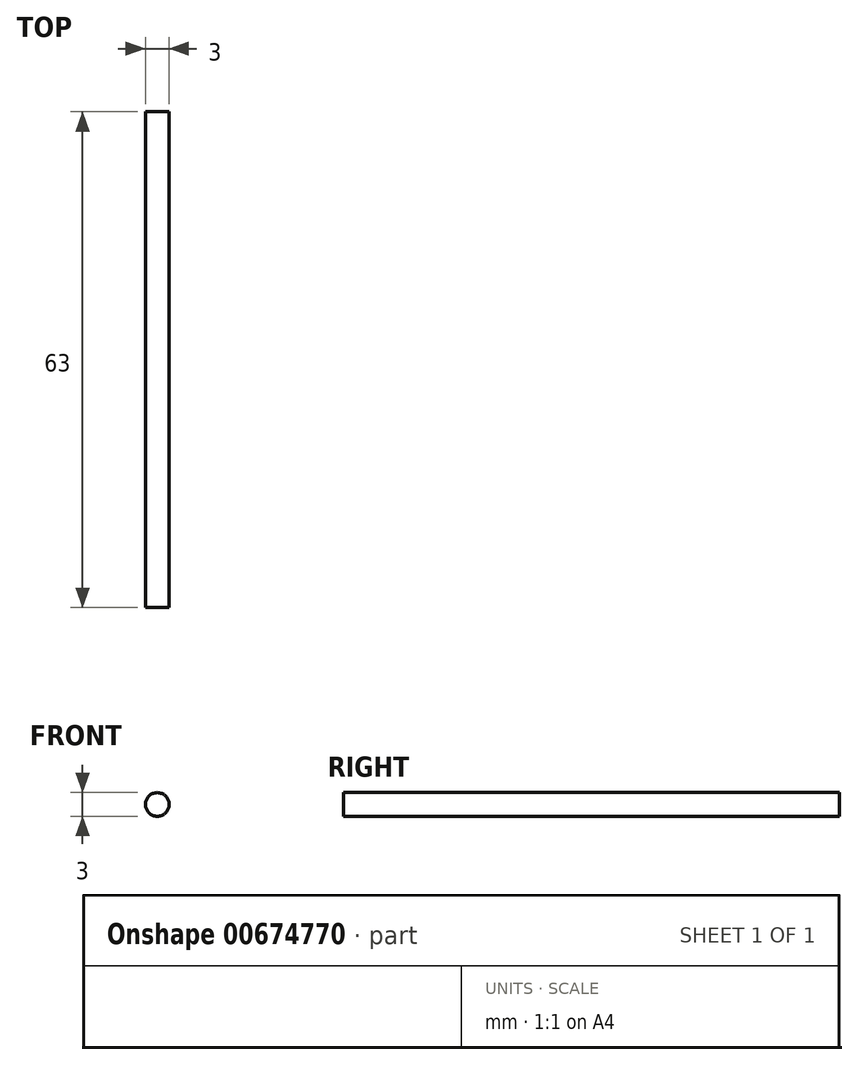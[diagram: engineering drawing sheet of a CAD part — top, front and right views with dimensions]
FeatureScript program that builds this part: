
annotation { "Feature Type Name" : "Feature", "Feature Type Description" : "" }
export const myFeature = defineFeature(function(context is Context, id is Id, definition is map)
    precondition{}
    {
        {
            var Q0;
            Q0=qCreatedBy(makeId("Front.planeOp"),FACE);
            var sketch = newSketch(context, id + "F0", { "sketchPlane" : qUnion([Q0])});
            skCircle(sketch, "E0", {"center": v(0, 0) * mm, "radius": 1.5 * mm});
            skSolve(sketch);
        }
        {
            var Q0;
            Q0=makeQuery(id+"F0.imprint","IMPRINT",FACE,{"disambiguationData":[TD([[makeQuery(id+"F0.imprint","IMPRINT",EDGE,{"derivedFrom":sQuery(id+"F0.wireOp",EDGE,"E0")}),1.0]])]});
            extrude(context, id + "F1", {"entities" : qUnion([Q0]), "oppositeDirection" : true, "depth" : 63 * mm, "offsetDistance" : 25.4 * mm});
        }
    });
